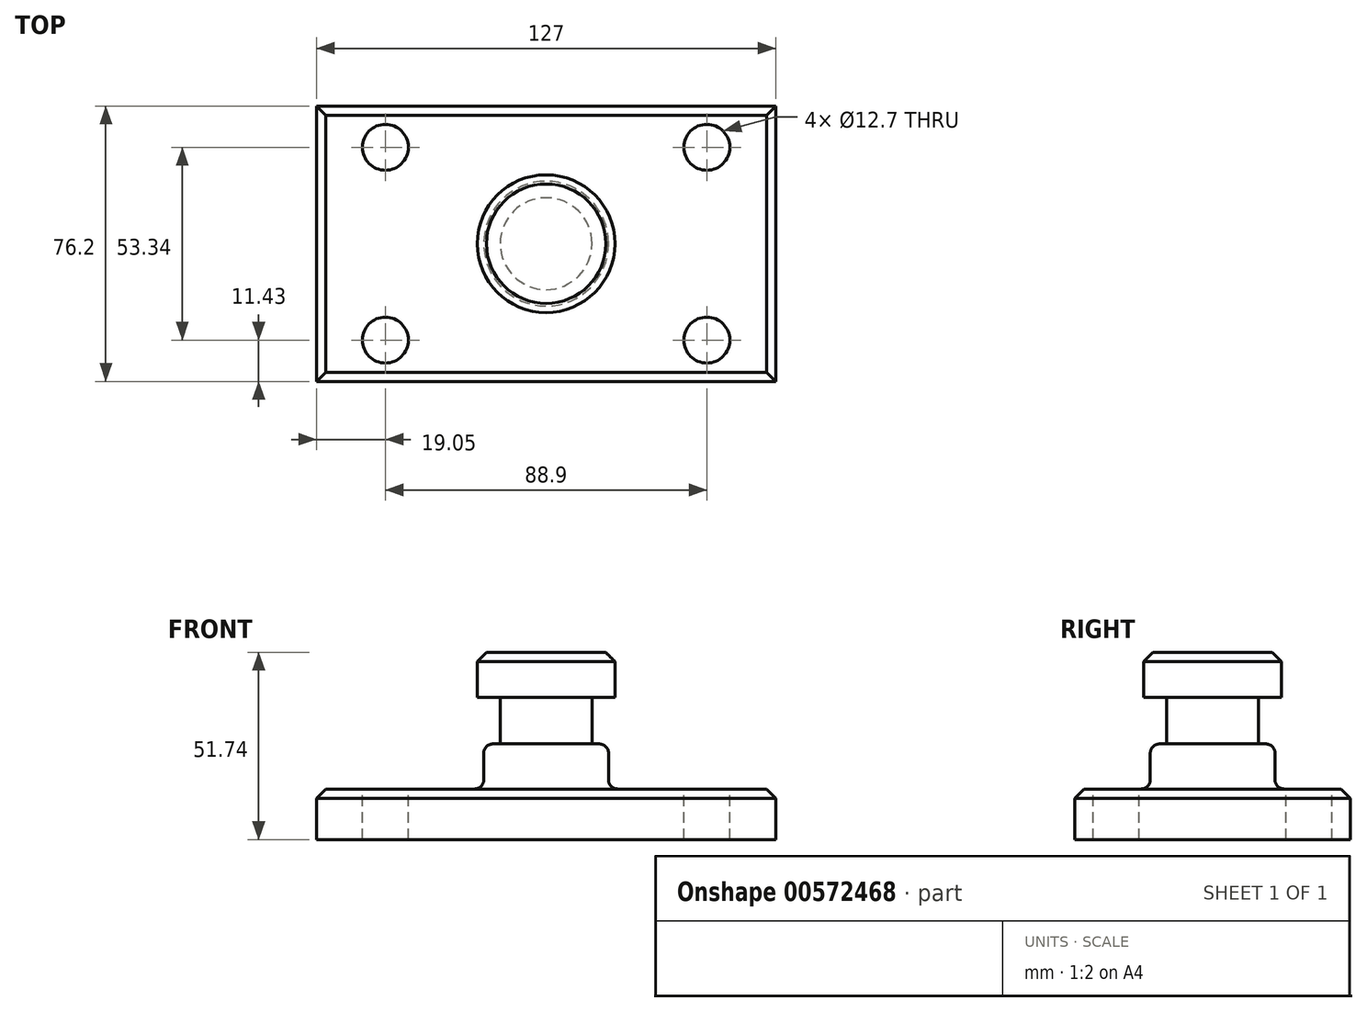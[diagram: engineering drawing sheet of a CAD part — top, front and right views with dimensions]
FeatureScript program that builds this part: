
annotation { "Feature Type Name" : "Feature", "Feature Type Description" : "" }
export const myFeature = defineFeature(function(context is Context, id is Id, definition is map)
    precondition{}
    {
        {
            var Q0;
            Q0=qCreatedBy(makeId("Top.planeOp"),FACE);
            var sketch = newSketch(context, id + "F0", { "sketchPlane" : qUnion([Q0])});
            skPoint(sketch, "E0.middle", {"position": v(0, 0) * mm});
            skLineSegment(sketch, "E1.bottom", {"start": v(-63.5, 38.1) * mm, "end": v(63.5, 38.1) * mm});
            skLineSegment(sketch, "E1.top", {"start": v(-63.5, -38.1) * mm, "end": v(63.5, -38.1) * mm});
            skLineSegment(sketch, "E1.left", {"start": v(-63.5, 38.1) * mm, "end": v(-63.5, -38.1) * mm});
            skLineSegment(sketch, "E1.right", {"start": v(63.5, 38.1) * mm, "end": v(63.5, -38.1) * mm});
            skSolve(sketch);
        }
        {
            var Q0;
            Q0 = qSketchRegion(id + "F0", true);
            extrude(context, id + "F1", {"entities" : qUnion([Q0]), "depth" : 13.97 * mm, "offsetDistance" : 25.4 * mm});
        }
        {
            var Q0;
            Q0=makeQuery(id+"F1.opExtrude","CAP_FACE",FACE,{"disambiguationData":[OSD([sQuery(id+"F0.wireOp",EDGE,"E1.bottom"),sQuery(id+"F0.wireOp",EDGE,"E1.top"),sQuery(id+"F0.wireOp",EDGE,"E1.left"),sQuery(id+"F0.wireOp",EDGE,"E1.right")])],"isStart":false});
            var sketch = newSketch(context, id + "F2", { "sketchPlane" : qUnion([Q0])});
            skCircle(sketch, "E2", {"center": v(-44.45, 26.67) * mm, "radius": 6.35 * mm});
            skCircle(sketch, "E3", {"center": v(44.45, 26.67) * mm, "radius": 6.35 * mm});
            skCircle(sketch, "E4", {"center": v(-44.45, -26.67) * mm, "radius": 6.35 * mm});
            skCircle(sketch, "E5", {"center": v(44.45, -26.67) * mm, "radius": 6.35 * mm});
            skSolve(sketch);
        }
        {
            var Q0;
            Q0=sQuery(id+"F2.wireOp",VERTEX,"E2.center");
            var Q1;
            Q1=sQuery(id+"F2.wireOp",VERTEX,"E4.center");
            var Q2;
            Q2=sQuery(id+"F2.wireOp",VERTEX,"E3.center");
            var Q3;
            Q3=sQuery(id+"F2.wireOp",VERTEX,"E5.center");
            var Q4;
            Q4=makeQuery(id+"F1.opExtrude","SWEPT_BODY",BODY,{"disambiguationData":[OSD([sQuery(id+"F0.wireOp",EDGE,"E1.bottom"),sQuery(id+"F0.wireOp",EDGE,"E1.top"),sQuery(id+"F0.wireOp",EDGE,"E1.left"),sQuery(id+"F0.wireOp",EDGE,"E1.right")])]});
            hole(context, id + "F3", {"style" : HoleStyle.SIMPLE, "endStyle" : HoleEndStyle.THROUGH, "holeDiameter" : 12.7 * mm, "isTappedThrough" : true, "tappedDepth" : 12.7 * mm, "tapClearance" : 3, "locations" : qUnion([Q0, Q1, Q2, Q3]), "scope" : qUnion([Q4])});
        }
        {
            var Q0;
            Q0=qCreatedBy(makeId("Front.planeOp"),FACE);
            var sketch = newSketch(context, id + "F4", { "sketchPlane" : qUnion([Q0])});
            skLineSegment(sketch, "E6.bottom", {"start": v(0, 39.37) * mm, "end": v(12.7, 39.37) * mm});
            skLineSegment(sketch, "E6.top", {"start": v(0, 13.97) * mm, "end": v(12.7, 13.97) * mm});
            skLineSegment(sketch, "E6.left", {"start": v(0, 39.37) * mm, "end": v(0, 13.97) * mm});
            skLineSegment(sketch, "E6.right", {"start": v(12.7, 39.37) * mm, "end": v(12.7, 13.97) * mm});
            skSolve(sketch);
        }
        {
            var Q0;
            Q0 = qSketchRegion(id + "F4", true);
            var Q1;
            Q1=sQuery(id+"F4.wireOp",EDGE,"E6.left");
            revolve(context, id + "F5", {"operationType" : NewBodyOperationType.ADD, "entities" : qUnion([Q0]), "axis" : qUnion([Q1]), "revolveType" : RevolveType.FULL});
        }
        {
            var Q0;
            Q0=qCreatedBy(makeId("Front.planeOp"),FACE);
            var sketch = newSketch(context, id + "F6", { "sketchPlane" : qUnion([Q0])});
            skLineSegment(sketch, "E7.bottom", {"start": v(0, 51.74) * mm, "end": v(19.05, 51.74) * mm});
            skLineSegment(sketch, "E7.top", {"start": v(0, 39.37) * mm, "end": v(19.05, 39.37) * mm});
            skLineSegment(sketch, "E7.left", {"start": v(0, 51.74) * mm, "end": v(0, 39.37) * mm});
            skLineSegment(sketch, "E7.right", {"start": v(19.05, 51.74) * mm, "end": v(19.05, 39.37) * mm});
            skSolve(sketch);
        }
        {
            var Q0;
            Q0=makeQuery(id+"F6.imprint","IMPRINT",FACE,{"disambiguationData":[TD([[makeQuery(id+"F6.imprint","IMPRINT",EDGE,{"derivedFrom":sQuery(id+"F6.wireOp",EDGE,"E7.bottom")}),-1.0]])]});
            var Q1;
            Q1=sQuery(id+"F6.wireOp",EDGE,"E7.left");
            revolve(context, id + "F7", {"operationType" : NewBodyOperationType.ADD, "entities" : qUnion([Q0]), "axis" : qUnion([Q1]), "revolveType" : RevolveType.FULL});
        }
        {
            var Q0;
            Q0=qCreatedBy(makeId("Front.planeOp"),FACE);
            var sketch = newSketch(context, id + "F8", { "sketchPlane" : qUnion([Q0])});
            skLineSegment(sketch, "E8.bottom", {"start": v(17.25, 13.97) * mm, "end": v(7.67, 13.97) * mm});
            skLineSegment(sketch, "E8.top", {"start": v(17.25, 26.43) * mm, "end": v(7.67, 26.43) * mm});
            skLineSegment(sketch, "E8.left", {"start": v(17.25, 13.97) * mm, "end": v(17.25, 26.43) * mm});
            skLineSegment(sketch, "E8.right", {"start": v(7.67, 13.97) * mm, "end": v(7.67, 26.43) * mm});
            skPoint(sketch, "E8.middle", {"position": v(12.46, 20.2) * mm});
            skSolve(sketch);
        }
        {
            var Q0;
            Q0 = qSketchRegion(id + "F8", true);
            var Q1;
            Q1=makeQuery(id+"F5.opRevolve","SWEPT_FACE",FACE,{"disambiguationData":[OSD([sQuery(id+"F4.wireOp",EDGE,"E6.right")])]});
            revolve(context, id + "F9", {"operationType" : NewBodyOperationType.ADD, "entities" : qUnion([Q0]), "axis" : qUnion([Q1]), "revolveType" : RevolveType.FULL});
        }
        {
            var Q0;
            Q0=makeQuery(id+"F9.opRevolve","SWEPT_EDGE",EDGE,{"disambiguationData":[OSD([sQuery(id+"F8.wireOp",EDGE,"E8.top"),sQuery(id+"F8.wireOp",EDGE,"E8.left")])]});
            var Q1;
            Q1=makeQuery(id+"F9.opRevolve","SWEPT_FACE",FACE,{"disambiguationData":[OSD([sQuery(id+"F8.wireOp",EDGE,"E8.left")])]});
            fillet(context, id + "F10", {"entities" : qUnion([Q0, Q1]), "radius" : 2.54 * mm, "tangentPropagation" : true, "allowEdgeOverflow" : false});
        }
        {
            var Q0;
            Q0=makeQuery(id+"F7.opRevolve","SWEPT_EDGE",EDGE,{"disambiguationData":[OSD([sQuery(id+"F6.wireOp",EDGE,"E7.bottom"),sQuery(id+"F6.wireOp",EDGE,"E7.right")])]});
            chamfer(context, id + "F11", {"entities" : qUnion([Q0]), "width" : 2.54 * mm, "tangentPropagation" : true});
        }
        {
            var Q0;
            Q0=makeQuery(id+"F1.opExtrude","CAP_EDGE",EDGE,{"disambiguationData":[OSD([sQuery(id+"F0.wireOp",EDGE,"E1.top")])],"isStart":false});
            var Q1;
            Q1=makeQuery(id+"F1.opExtrude","CAP_EDGE",EDGE,{"disambiguationData":[OSD([sQuery(id+"F0.wireOp",EDGE,"E1.left")])],"isStart":false});
            var Q2;
            Q2=makeQuery(id+"F1.opExtrude","CAP_EDGE",EDGE,{"disambiguationData":[OSD([sQuery(id+"F0.wireOp",EDGE,"E1.bottom")])],"isStart":false});
            var Q3;
            Q3=makeQuery(id+"F1.opExtrude","CAP_EDGE",EDGE,{"disambiguationData":[OSD([sQuery(id+"F0.wireOp",EDGE,"E1.right")])],"isStart":false});
            chamfer(context, id + "F12", {"entities" : qUnion([Q0, Q1, Q2, Q3]), "width" : 2.54 * mm, "tangentPropagation" : true});
        }
    });
